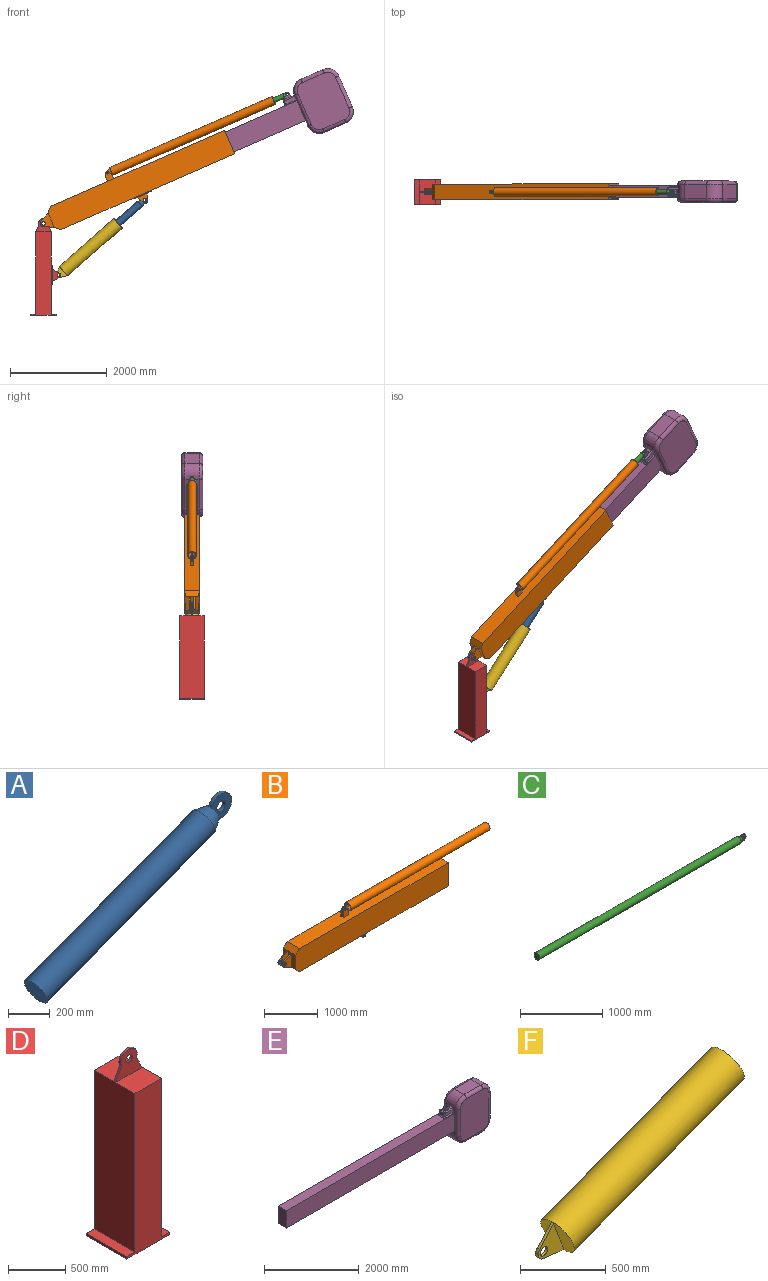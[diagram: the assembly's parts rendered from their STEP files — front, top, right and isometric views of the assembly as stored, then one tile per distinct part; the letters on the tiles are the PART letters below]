
ASSEMBLY  parts=6 mates=7
PART A: 9 faces, bbox 1339.2x146.3x607.4 mm
  f0: plane 79.65x33.73mm, normal (0.94,0,0.35), area 2136.8mm2, adj f4,f5
  f1: plane 79.65x33.73mm, normal (0.94,0,0.35), area 2136.8mm2, adj f4,f8
  f2: cylinder r=73.12mm len=1183.03mm, axis (-0.94,0,-0.35), area 555656.9mm2, adj f3,f4
  f3: plane 146.25x136.81mm, normal (-0.94,0,-0.35), area 16798.9mm2, adj f2
  f4: cone r=43.73mm half-angle=25deg, axis (-0.94,0,-0.35), area 25411.6mm2, adj f0,f1,f2,f5,f6,f8
  f5: plane 146.03x141.59mm, normal (0,-1,0), area 11416.2mm2, adj f0,f4,f6,f7
  f6: cylinder r=70.11mm len=140.22mm, axis (0,1,0), area 6879.1mm2, adj f4,f5,f8
  f7: cylinder r=30mm len=60mm, axis (0,-1,0), area 3769.9mm2, adj f5,f8
  f8: plane 146.03x141.59mm, normal (0,1,0), area 11416.2mm2, adj f1,f4,f6,f7
PART B: 73 faces, bbox 5442.9x325x954.4 mm
  f0: plane 327.48x100mm, normal (-1,0,0), area 32748.1mm2, adj f29,f30,f33,f65
  f1: plane 327.48x75mm, normal (-1,0,0), area 24561.1mm2, adj f29,f33,f66,f67
  f2: plane 327.48x100mm, normal (-1,0,0), area 32748.1mm2, adj f29,f32,f33,f68
  f3: plane 226.21x161.25mm, normal (0,-1,0), area 19899.8mm2, adj f4,f5,f6,f7,f19
  f4: plane 134.9x69.81mm, normal (-0.89,0,-0.46), area 2848mm2, adj f3,f7,f8,f19
  f5: cylinder r=30mm len=60mm, axis (0,-1,0), area 3534.3mm2, adj f3,f8
  f6: plane 134.9x69.81mm, normal (0.89,0,-0.46), area 2848mm2, adj f3,f7,f8,f19
  f7: cylinder r=48.75mm len=86.59mm, axis (0,1,0), area 1998.7mm2, adj f3,f4,f6,f8
  f8: plane 226.21x161.25mm, normal (0,1,0), area 19899.8mm2, adj f4,f5,f6,f7,f19
  f9: plane 226.21x161.25mm, normal (0,-1,0), area 19899.8mm2, adj f10,f11,f12,f13,f19
  f10: plane 134.9x69.81mm, normal (-0.89,0,-0.46), area 2848mm2, adj f9,f13,f14,f19
  f11: cylinder r=30mm len=60mm, axis (0,-1,0), area 3534.3mm2, adj f9,f14
  f12: plane 134.9x69.81mm, normal (0.89,0,-0.46), area 2848mm2, adj f9,f13,f14,f19
  f13: cylinder r=48.75mm len=86.59mm, axis (0,1,0), area 1998.7mm2, adj f9,f10,f12,f14
  f14: plane 226.21x161.25mm, normal (0,1,0), area 19899.8mm2, adj f10,f11,f12,f13,f19
  f15: plane 243.75x18.75mm, normal (-1,0,0), area 4570.3mm2, adj f16,f18,f19,f31
  f16: plane 395.61x18.75mm, normal (0,-1,0), area 7417.7mm2, adj f15,f17,f19,f31
  f17: plane 243.75x18.75mm, normal (1,0,0), area 4570.3mm2, adj f16,f18,f19,f31
  f18: plane 395.61x18.75mm, normal (0,1,0), area 7417.7mm2, adj f15,f17,f19,f31
  f19: plane 395.61x243.75mm, normal (0,0,-1), area 87947.4mm2, adj f3,f4,f6,f8,f9,f10,f12,f14
  f20: plane 3925x325mm, normal (0,0,1), area 1267209.6mm2, adj f28,f29,f30,f32,f57,f58,f59,f60
  f21: plane 3914.64x275mm, normal (0,0,-1), area 1076527.3mm2, adj f22,f23,f25,f28
  f22: plane 275x85.36mm, normal (0.71,0,-0.71), area 33195.4mm2, adj f21,f23,f25,f27
  f23: plane 4000x477.48mm, normal (0,-1,0), area 1902638.7mm2, adj f21,f22,f24,f26,f27,f28
  f24: plane 3914.64x275mm, normal (0,0,1), area 1076527.3mm2, adj f23,f25,f26,f28
  f25: plane 4000x477.48mm, normal (0,1,0), area 1902638.7mm2, adj f21,f22,f24,f26,f27,f28
  f26: plane 275x85.36mm, normal (0.71,0,0.71), area 33195.4mm2, adj f23,f24,f25,f27
  f27: plane 306.77x275mm, normal (1,0,0), area 84361.9mm2, adj f22,f23,f25,f26
  f28: plane 527.48x325mm, normal (1,0,0), area 40124.1mm2, adj f20,f21,f23,f24,f25,f30,f31,f32
  f29: plane 325x100mm, normal (-0.71,0,0.71), area 45961.9mm2, adj f0,f1,f2,f20,f30,f32,f62,f71
  f30: plane 4025x527.48mm, normal (0,1,0), area 2113111.3mm2, adj f0,f20,f28,f29,f31,f33
  f31: plane 3925x325mm, normal (0,0,-1), area 1179194.9mm2, adj f15,f16,f17,f18,f28,f30,f32,f33
  f32: plane 4025x527.48mm, normal (0,-1,0), area 2113111.3mm2, adj f2,f20,f28,f29,f31,f33
  f33: plane 325x100mm, normal (-0.71,0,-0.71), area 45961.9mm2, adj f0,f1,f2,f30,f31,f32,f64,f69
  f34: cylinder r=75mm len=3664.82mm, axis (1,0,0), area 1726946mm2, adj f35,f36,f39,f46,f47
  f35: plane 175x175mm, normal (1,0,0), area 6381.4mm2, adj f34,f37
  f36: plane 175x175mm, normal (-1,0,0), area 6324.4mm2, adj f34,f37,f38,f39,f47
  f37: cylinder r=87.5mm len=3664.82mm, axis (-1,0,0), area 2014837.9mm2, adj f35,f36
  f38: plane 97.8x50.61mm, normal (-0.46,0,0.89), area 1376.5mm2, adj f36,f39,f47,f48
  f39: plane 138.86x120mm, normal (0,1,0), area 10294.4mm2, adj f34,f36,f38,f45,f46,f48,f49,f50
  f40: plane 74.32x38.46mm, normal (-0.89,0,0.46), area 1046.1mm2, adj f41,f43,f58,f59
  f41: cylinder r=32.5mm len=57.73mm, axis (0,-1,0), area 888.3mm2, adj f40,f43,f44,f58
  f42: cylinder r=20mm len=40mm, axis (0,1,0), area 1570.8mm2, adj f43,f58
  f43: plane 134.65x91.89mm, normal (0,1,0), area 6616.1mm2, adj f40,f41,f42,f44,f56
  f44: plane 74.32x38.46mm, normal (0.89,0,0.46), area 1046.1mm2, adj f41,f43,f57,f58
  f45: plane 20.18x12.5mm, normal (0,0,-1), area 252.2mm2, adj f39,f46,f47,f57
  f46: plane 134.39x12.5mm, normal (1,0,0), area 1678.8mm2, adj f34,f39,f45,f47
  f47: plane 138.86x120mm, normal (0,-1,0), area 10294.4mm2, adj f34,f36,f38,f45,f46,f48,f49,f50
  f48: cylinder r=32.5mm len=57.73mm, axis (0,1,0), area 888.3mm2, adj f38,f39,f47,f49
  f49: plane 58.99x30.52mm, normal (-0.46,0,-0.89), area 830.2mm2, adj f39,f47,f48,f56
  f50: cylinder r=20mm len=40mm, axis (0,-1,0), area 1570.8mm2, adj f39,f47
  f51: plane 134.65x91.89mm, normal (0,-1,0), area 6616.1mm2, adj f52,f53,f54,f55,f56
  f52: plane 74.32x38.46mm, normal (-0.89,0,0.46), area 1046.1mm2, adj f51,f53,f59,f60
  f53: cylinder r=32.5mm len=57.73mm, axis (0,-1,0), area 888.3mm2, adj f51,f52,f55,f60
  f54: cylinder r=20mm len=40mm, axis (0,1,0), area 1570.8mm2, adj f51,f60
  f55: plane 74.32x38.46mm, normal (0.89,0,0.46), area 1046.1mm2, adj f51,f53,f57,f60
  f56: plane 134.65x37.5mm, normal (0,0,1), area 4758.4mm2, adj f39,f43,f47,f49,f51,f57,f59
  f57: plane 100x62.5mm, normal (1,0,0), area 6250mm2, adj f20,f44,f45,f55,f56,f58,f60
  f58: plane 191.89x134.65mm, normal (0,-1,0), area 20080.8mm2, adj f20,f40,f41,f42,f44,f57,f59
  f59: plane 100x62.5mm, normal (-1,0,0), area 6250mm2, adj f20,f40,f52,f56,f58,f60
  f60: plane 191.89x134.65mm, normal (0,1,0), area 20080.8mm2, adj f20,f52,f53,f54,f55,f57,f59
  f61: cylinder r=40mm len=80mm, axis (0,1,0), area 6283.2mm2, adj f65,f66
  f62: plane 204.87x106.01mm, normal (-0.46,0,0.89), area 5766.9mm2, adj f29,f63,f65,f66
  f63: cylinder r=65mm len=115.46mm, axis (0,-1,0), area 3553.2mm2, adj f62,f64,f65,f66
  f64: plane 204.87x106.01mm, normal (-0.46,0,-0.89), area 5766.9mm2, adj f33,f63,f65,f66
  f65: plane 327.48x240mm, normal (0,1,0), area 43241.1mm2, adj f0,f61,f62,f63,f64
  f66: plane 327.48x240mm, normal (0,-1,0), area 43241.1mm2, adj f1,f61,f62,f63,f64
  f67: plane 327.48x240mm, normal (0,1,0), area 43241.1mm2, adj f1,f69,f70,f71,f72
  f68: plane 327.48x240mm, normal (0,-1,0), area 43241.1mm2, adj f2,f69,f70,f71,f72
  f69: plane 204.87x106.01mm, normal (-0.46,0,-0.89), area 5766.9mm2, adj f33,f67,f68,f70
  f70: cylinder r=65mm len=115.46mm, axis (0,-1,0), area 3553.2mm2, adj f67,f68,f69,f71
  f71: plane 204.87x106.01mm, normal (-0.46,0,0.89), area 5766.9mm2, adj f29,f67,f68,f70
  f72: cylinder r=40mm len=80mm, axis (0,1,0), area 6283.2mm2, adj f67,f68
PART C: 9 faces, bbox 3589.5x97.5x100.1 mm
  f0: plane 56.76x22.49mm, normal (1,0,0), area 949.7mm2, adj f2,f3
  f1: plane 56.76x22.49mm, normal (1,0,0), area 949.7mm2, adj f2,f6
  f2: cone r=29.15mm half-angle=25deg, axis (-1,0,0), area 11294mm2, adj f0,f1,f3,f4,f6,f8
  f3: plane 100.09x83.11mm, normal (0,-1,0), area 5073.9mm2, adj f0,f2,f4,f5
  f4: cylinder r=46.74mm len=93.48mm, axis (0,1,0), area 3057.4mm2, adj f2,f3,f6
  f5: cylinder r=20mm len=40mm, axis (0,-1,0), area 1675.5mm2, adj f3,f6
  f6: plane 100.09x83.11mm, normal (0,1,0), area 5073.9mm2, adj f1,f2,f4,f5
  f7: plane 97.5x97.5mm, normal (-1,0,0), area 7466.2mm2, adj f8
  f8: cylinder r=48.75mm len=3466.44mm, axis (-1,0,0), area 1061787.3mm2, adj f2,f7
PART D: 34 faces, bbox 626.2x500x2000 mm
  f0: cylinder r=40mm len=80mm, axis (0,-1,0), area 6283.2mm2, adj f4,f5
  f1: plane 137.38x71.09mm, normal (0.89,0,0.46), area 3867mm2, adj f3,f4,f5,f31
  f2: plane 137.38x71.09mm, normal (-0.89,0,0.46), area 3867mm2, adj f3,f4,f5,f32
  f3: cylinder r=100mm len=200mm, axis (0,1,0), area 9782.5mm2, adj f1,f2,f4,f5
  f4: plane 327.48x275mm, normal (0,-1,0), area 53247.3mm2, adj f0,f1,f2,f3,f7
  f5: plane 327.48x275mm, normal (0,1,0), area 53247.3mm2, adj f0,f1,f2,f3,f6
  f6: plane 327.48x237.5mm, normal (0,0,1), area 77776.8mm2, adj f5,f30,f31,f32
  f7: plane 327.48x237.5mm, normal (0,0,1), area 77776.8mm2, adj f4,f31,f32,f33
  f8: cylinder r=30mm len=60mm, axis (0,1,0), area 3534.3mm2, adj f12,f13
  f9: plane 153.65x79.51mm, normal (0.46,0,-0.89), area 3243.9mm2, adj f10,f12,f13,f24
  f10: cylinder r=48.75mm len=86.59mm, axis (0,-1,0), area 1998.7mm2, adj f9,f11,f12,f13
  f11: plane 153.65x79.51mm, normal (0.46,0,0.89), area 3243.9mm2, adj f10,f12,f13,f24
  f12: plane 245.61x180mm, normal (0,1,0), area 24323.1mm2, adj f8,f9,f10,f11,f24
  f13: plane 245.61x180mm, normal (0,-1,0), area 24323.1mm2, adj f8,f9,f10,f11,f24
  f14: cylinder r=30mm len=60mm, axis (0,1,0), area 3534.3mm2, adj f18,f19
  f15: plane 153.65x79.51mm, normal (0.46,0,-0.89), area 3243.9mm2, adj f16,f18,f19,f24
  f16: cylinder r=48.75mm len=86.59mm, axis (0,-1,0), area 1998.7mm2, adj f15,f17,f18,f19
  f17: plane 153.65x79.51mm, normal (0.46,0,0.89), area 3243.9mm2, adj f16,f18,f19,f24
  f18: plane 245.61x180mm, normal (0,-1,0), area 24323.1mm2, adj f14,f15,f16,f17,f24
  f19: plane 245.61x180mm, normal (0,1,0), area 24323.1mm2, adj f14,f15,f16,f17,f24
  f20: plane 243.75x18.75mm, normal (0,0,1), area 4570.3mm2, adj f21,f23,f24,f31
  f21: plane 395.61x18.75mm, normal (0,-1,0), area 7417.7mm2, adj f20,f22,f24,f31
  f22: plane 243.75x18.75mm, normal (0,0,-1), area 4570.3mm2, adj f21,f23,f24,f31
  f23: plane 395.61x18.75mm, normal (0,1,0), area 7417.7mm2, adj f20,f22,f24,f31
  f24: plane 395.61x243.75mm, normal (1,0,0), area 87219.7mm2, adj f9,f11,f12,f13,f15,f17,f18,f19
  f25: plane 500x100mm, normal (0,0,1), area 50000mm2, adj f28,f30,f31,f33
  f26: plane 500x25mm, normal (-1,0,0), area 12500mm2, adj f27,f29,f30,f33
  f27: plane 527.48x500mm, normal (0,0,-1), area 263740.5mm2, adj f26,f28,f30,f33
  f28: plane 500x25mm, normal (1,0,0), area 12500mm2, adj f25,f27,f30,f33
  f29: plane 500x100mm, normal (0,0,1), area 50000mm2, adj f26,f30,f32,f33
  f30: plane 1725x527.48mm, normal (0,1,0), area 569904.8mm2, adj f6,f25,f26,f27,f28,f29,f31,f32
  f31: plane 1700x500mm, normal (1,0,0), area 753569.9mm2, adj f1,f6,f7,f20,f21,f22,f23,f25
  f32: plane 1700x500mm, normal (-1,0,0), area 850000mm2, adj f2,f6,f7,f29,f30,f33
  f33: plane 1725x527.48mm, normal (0,-1,0), area 569904.8mm2, adj f7,f25,f26,f27,f28,f29,f31,f32
PART E: 59 faces, bbox 6025x443.8x1200 mm
  f0: revolved ~291.38x254mm, area 116253.5mm2, adj f2,f5,f6,f13
  f1: revolved ~492x76.2mm, area 58889.8mm2, adj f2,f13,f14,f18
  f2: revolved ~254x254mm, area 42550mm2, adj f0,f1,f3,f18
  f3: revolved ~692x76.2mm, area 82828.7mm2, adj f2,f4,f5,f18
  f4: revolved ~254x254mm, area 42550mm2, adj f3,f18,f19,f20
  f5: plane 692x291.38mm, normal (1,0,0), area 201631.6mm2, adj f0,f3,f9,f20
  f6: revolved ~254x254mm, area 42550mm2, adj f0,f7,f9,f22
  f7: revolved ~492x76.2mm, area 58889.8mm2, adj f6,f12,f13,f22
  f8: revolved ~254x254mm, area 42550mm2, adj f9,f20,f21,f22
  f9: revolved ~692x76.2mm, area 82828.7mm2, adj f5,f6,f8,f22
  f10: revolved ~50.8x50.8mm, area 2170.3mm2, adj f16,f17,f23,f27
  f11: plane 446.26x243.78mm, normal (-1,0,0), area 108786.2mm2, adj f24,f25,f26,f27
  f12: revolved ~254x254mm, area 42550mm2, adj f7,f22,f28,f29
  f13: plane 492x291.38mm, normal (0,0,-1), area 143356.6mm2, adj f0,f1,f7,f29
  f14: revolved ~254x254mm, area 42550mm2, adj f1,f18,f29,f30
  f15: revolved ~50.8x50.8mm, area 2170.3mm2, adj f16,f27,f31,f32
  f16: revolved ~111.7x25.4mm, area 4456.6mm2, adj f10,f15,f27,f33
  f17: revolved ~74.2x25.4mm, area 2960.4mm2, adj f10,f33,f34,f35
  f18: plane 1047.6x847.6mm, normal (0,-1,0), area 860808.9mm2, adj f1,f2,f3,f4,f14,f19,f30,f36
  f19: revolved ~492x76.2mm, area 58889.8mm2, adj f4,f18,f36,f37
  f20: revolved ~291.38x254mm, area 116253.5mm2, adj f4,f5,f8,f37
  f21: revolved ~492x76.2mm, area 58889.8mm2, adj f8,f22,f37,f38
  f22: plane 1047.6x847.6mm, normal (0,1,0), area 860808.9mm2, adj f6,f7,f8,f9,f12,f21,f28,f38
  f23: revolved ~238.34x25.4mm, area 9509.4mm2, adj f10,f27,f35,f40
  f24: plane 5025x446.26mm, normal (0,-1,0), area 2242437.5mm2, adj f11,f25,f27,f40
  f25: plane 5025x243.78mm, normal (0,0,-1), area 1224970.1mm2, adj f11,f24,f26,f40
  f26: plane 5025x446.26mm, normal (0,1,0), area 2242437.5mm2, adj f11,f25,f27,f40
  f27: plane 5025.01x243.78mm, normal (0,0,1), area 1164404.7mm2, adj f10,f11,f15,f16,f23,f24,f26,f32
  f28: revolved ~692x76.2mm, area 82828.7mm2, adj f12,f22,f38,f40
  f29: revolved ~291.38x254mm, area 116253.5mm2, adj f12,f13,f14,f40
  f30: revolved ~692x76.2mm, area 82828.7mm2, adj f14,f18,f36,f40
  f31: revolved ~74.2x25.4mm, area 2960.4mm2, adj f15,f33,f39,f41
  f32: revolved ~238.34x25.4mm, area 9509.4mm2, adj f15,f27,f40,f41
  f33: plane 111.7x74.2mm, normal (-1,0,0), area 8288.1mm2, adj f16,f17,f31,f44
  f34: revolved ~25.4x25.4mm, area 1013.4mm2, adj f17,f44,f45
  f35: plane 238.34x74.2mm, normal (0,-1,0), area 17684.9mm2, adj f17,f23,f40,f45
  f36: revolved ~254x254mm, area 42550mm2, adj f18,f19,f30,f46
  f37: plane 492x291.38mm, normal (0,0,1), area 143356.6mm2, adj f19,f20,f21,f46
  f38: revolved ~254x254mm, area 42550mm2, adj f21,f22,f28,f46
  f39: revolved ~25.4x25.4mm, area 1013.4mm2, adj f31,f44,f47
  f40: plane 692x291.38mm, normal (-1,0,0), area 72802.5mm2, adj f23,f24,f25,f26,f27,f28,f29,f30
  f41: plane 238.34x74.2mm, normal (0,1,0), area 17684.9mm2, adj f31,f32,f40,f47
  f42: revolved ~57.73x17.56mm, area 888.3mm2, adj f48,f49,f50,f51
  f43: revolved ~40x40mm, area 3141.6mm2, adj f49,f51
  f44: revolved ~111.7x25.4mm, area 4456.6mm2, adj f33,f34,f39,f54
  f45: revolved ~238.35x25.4mm, area 9509.4mm2, adj f34,f35,f40,f46,f54
  f46: revolved ~291.38x254mm, area 115990.4mm2, adj f36,f37,f38,f40,f45,f47,f54
  f47: revolved ~238.35x25.4mm, area 9509.4mm2, adj f39,f40,f41,f46,f54
  f48: plane 89.94x46.54mm, normal (0.89,0,0.46), area 1265.8mm2, adj f42,f49,f51,f54
  f49: plane 150.81x107.5mm, normal (0,-1,0), area 8844.4mm2, adj f42,f43,f48,f50,f54
  f50: plane 89.94x46.54mm, normal (-0.89,0,0.46), area 1265.8mm2, adj f42,f49,f51,f54
  f51: plane 150.81x107.5mm, normal (0,1,0), area 8844.4mm2, adj f42,f43,f48,f50,f54
  f52: plane 89.94x46.54mm, normal (0.89,0,0.46), area 1265.8mm2, adj f54,f55,f56,f58
  f53: revolved ~40x40mm, area 3141.6mm2, adj f55,f56
  f54: plane 238.35x111.7mm, normal (0,0,1), area 22853.5mm2, adj f44,f45,f46,f47,f48,f49,f50,f51
  f55: plane 150.81x107.5mm, normal (0,-1,0), area 8844.4mm2, adj f52,f53,f54,f57,f58
  f56: plane 150.81x107.5mm, normal (0,1,0), area 8844.4mm2, adj f52,f53,f54,f57,f58
  f57: plane 89.94x46.54mm, normal (-0.89,0,0.46), area 1265.8mm2, adj f54,f55,f56,f58
  f58: revolved ~57.73x17.56mm, area 888.3mm2, adj f52,f55,f56,f57
PART F: 11 faces, bbox 1621.1x262.5x775.6 mm
  f0: cylinder r=30mm len=60mm, axis (0,-1,0), area 3534.3mm2, adj f4,f5
  f1: plane 171.84x20.08mm, normal (-0.12,0,-0.99), area 3243.9mm2, adj f2,f4,f5,f10
  f2: cylinder r=48.75mm len=81.01mm, axis (0,1,0), area 1998.7mm2, adj f1,f3,f4,f5
  f3: plane 128.68x115.64mm, normal (-0.74,0,0.67), area 3243.9mm2, adj f2,f4,f5,f10
  f4: plane 229.76x214.93mm, normal (0,1,0), area 24323.1mm2, adj f0,f1,f2,f3,f10
  f5: plane 229.76x214.93mm, normal (0,-1,0), area 24323.1mm2, adj f0,f1,f2,f3,f10
  f6: cylinder r=112.5mm len=1465.19mm, axis (0.94,0,0.35), area 1047033.9mm2, adj f7,f9
  f7: plane 225x210.48mm, normal (0.94,0,0.35), area 39760.8mm2, adj f6
  f8: cylinder r=131.25mm len=1495.98mm, axis (-0.94,0,-0.35), area 1237002.1mm2, adj f9,f10
  f9: plane 262.5x245.56mm, normal (0.94,0,0.35), area 14358.1mm2, adj f6,f8
  f10: plane 262.5x245.56mm, normal (-0.94,0,-0.35), area 49513.6mm2, adj f1,f3,f4,f5,f8
PLACE A rot(axis=(0,-1,0),20.5deg) t=(4440.74,-18.8,1355.23)mm
PLACE B rot(axis=(0,-1,0),23.6deg) t=(4533.37,-20.5,1475.74)mm
PLACE C rot(axis=(0,-1,0),23.6deg) t=(1908.77,-20.5,328.01)mm
PLACE D rot(axis=(-0.5,-0.75,0.44),0deg) t=(3699.35,-19.7,-174.02)mm fixed
PLACE E rot(axis=(0,-1,0),23.6deg) t=(1908.77,-20.5,328.01)mm
PLACE F rot(axis=(0,-1,0),20.5deg) t=(4107.77,-18.8,1063.59)mm
MATE slider E.f11 <-> B.f28  axis (-0.92,0,-0.4) through (896.94,215.75,2962.61)mm
MATE revolute F.f0 <-> D.f10  axis (0,1,0) through (485,226.83,1572.96)mm
MATE cylindrical A.f6 <-> B.f5  axis (0,-1,0) through (2259.76,207.45,3127.47)mm
MATE slider A.f4 <-> F.f8  axis (-0.75,0,-0.66) through (1263.96,217.45,2255.25)mm
MATE cylindrical C.f4 <-> E.f51  axis (0,-1,0) through (5210.62,209.09,5310.79)mm
MATE slider C.f8 <-> B.f37  axis (-0.92,0,-0.4) through (1964.71,215.75,3891.36)mm
MATE revolute B.f63 <-> D.f3  axis (0,-1,0) through (171.26,153.25,2645.27)mm
